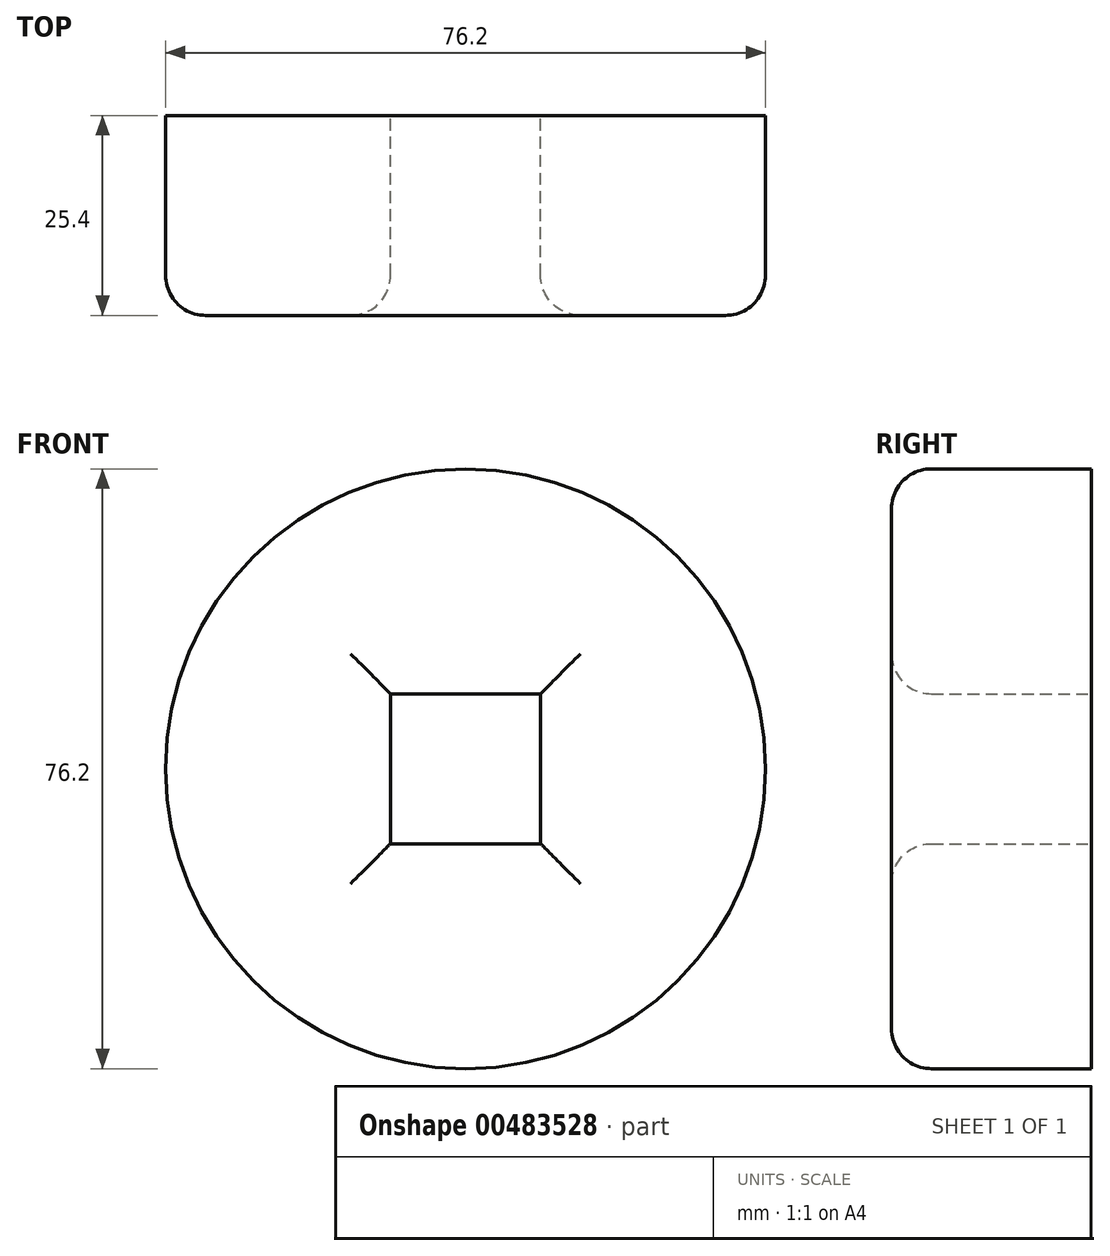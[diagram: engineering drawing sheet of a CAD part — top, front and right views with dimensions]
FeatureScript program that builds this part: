
annotation { "Feature Type Name" : "Feature", "Feature Type Description" : "" }
export const myFeature = defineFeature(function(context is Context, id is Id, definition is map)
    precondition{}
    {
        {
            var Q0;
            Q0=qCreatedBy(makeId("Front.planeOp"),FACE);
            var sketch = newSketch(context, id + "F0", { "sketchPlane" : qUnion([Q0])});
            skCircle(sketch, "E0", {"center": v(0, 0) * mm, "radius": 38.1 * mm});
            skSolve(sketch);
        }
        {
            var Q0;
            Q0=makeQuery(id+"F0.imprint","IMPRINT",FACE,{"disambiguationData":[TD([[makeQuery(id+"F0.imprint","IMPRINT",EDGE,{"derivedFrom":sQuery(id+"F0.wireOp",EDGE,"E0")}),1.0]])]});
            extrude(context, id + "F1", {"entities" : qUnion([Q0]), "depth" : 25.4 * mm});
        }
        {
            var Q0;
            Q0=makeQuery(id+"F1.opExtrude","CAP_EDGE",EDGE,{"disambiguationData":[OSD([sQuery(id+"F0.wireOp",EDGE,"E0")])],"isStart":false});
            fillet(context, id + "F2", {"entities" : qUnion([Q0]), "radius" : 5.08 * mm, "tangentPropagation" : true, "allowEdgeOverflow" : false});
        }
        {
            var Q0;
            Q0=makeQuery(id+"F1.opExtrude","CAP_FACE",FACE,{"disambiguationData":[OSD([sQuery(id+"F0.wireOp",EDGE,"E0")])],"isStart":true});
            var sketch = newSketch(context, id + "F3", { "sketchPlane" : qUnion([Q0])});
            skLineSegment(sketch, "E1.bottom", {"start": v(-9.53, 9.53) * mm, "end": v(9.53, 9.53) * mm});
            skLineSegment(sketch, "E1.top", {"start": v(-9.53, -9.53) * mm, "end": v(9.53, -9.53) * mm});
            skLineSegment(sketch, "E1.left", {"start": v(-9.53, 9.53) * mm, "end": v(-9.53, -9.53) * mm});
            skLineSegment(sketch, "E1.right", {"start": v(9.53, 9.53) * mm, "end": v(9.53, -9.53) * mm});
            skSolve(sketch);
        }
        {
            var Q0;
            Q0=makeQuery(id+"F3.imprint","IMPRINT",FACE,{"disambiguationData":[TD([[makeQuery(id+"F3.imprint","IMPRINT",EDGE,{"derivedFrom":sQuery(id+"F3.wireOp",EDGE,"E1.bottom")}),-1.0]])]});
            extrude(context, id + "F4", {"entities" : qUnion([Q0]), "operationType" : NewBodyOperationType.REMOVE, "endBound" : BoundingType.THROUGH_ALL, "oppositeDirection" : true, "depth" : 25.4 * mm});
        }
        {
            var Q0;
            Q0=makeQuery(id+"F4.boolean.opBoolean","INTERSECT",EDGE,{"derivedFrom":[makeQuery(id+"F1.opExtrude","CAP_FACE",FACE,{"disambiguationData":[OSD([sQuery(id+"F0.wireOp",EDGE,"E0")])],"isStart":false}),makeQuery(id+"F4.opExtrude","SWEPT_FACE",FACE,{"disambiguationData":[OSD([sQuery(id+"F3.wireOp",EDGE,"E1.bottom")])]})]});
            var Q1;
            Q1=makeQuery(id+"F4.boolean.opBoolean","INTERSECT",EDGE,{"derivedFrom":[makeQuery(id+"F1.opExtrude","CAP_FACE",FACE,{"disambiguationData":[OSD([sQuery(id+"F0.wireOp",EDGE,"E0")])],"isStart":false}),makeQuery(id+"F4.opExtrude","SWEPT_FACE",FACE,{"disambiguationData":[OSD([sQuery(id+"F3.wireOp",EDGE,"E1.right")])]})]});
            var Q2;
            Q2=makeQuery(id+"F4.boolean.opBoolean","INTERSECT",EDGE,{"derivedFrom":[makeQuery(id+"F1.opExtrude","CAP_FACE",FACE,{"disambiguationData":[OSD([sQuery(id+"F0.wireOp",EDGE,"E0")])],"isStart":false}),makeQuery(id+"F4.opExtrude","SWEPT_FACE",FACE,{"disambiguationData":[OSD([sQuery(id+"F3.wireOp",EDGE,"E1.top")])]})]});
            var Q3;
            Q3=makeQuery(id+"F4.boolean.opBoolean","INTERSECT",EDGE,{"derivedFrom":[makeQuery(id+"F1.opExtrude","CAP_FACE",FACE,{"disambiguationData":[OSD([sQuery(id+"F0.wireOp",EDGE,"E0")])],"isStart":false}),makeQuery(id+"F4.opExtrude","SWEPT_FACE",FACE,{"disambiguationData":[OSD([sQuery(id+"F3.wireOp",EDGE,"E1.left")])]})]});
            fillet(context, id + "F5", {"entities" : qUnion([Q0, Q1, Q2, Q3]), "radius" : 5.08 * mm, "allowEdgeOverflow" : false});
        }
    });
